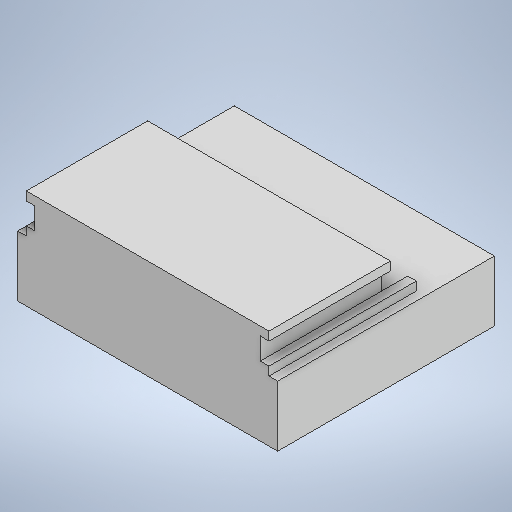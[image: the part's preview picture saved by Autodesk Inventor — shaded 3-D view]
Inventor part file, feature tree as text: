
AUTODESK INVENTOR PART (.ipt)
format: ipt  version: 2025.3 (Build 293356000, 356)  size: 224,768 bytes
history: native  units: mm
features: extrude x3, other x1, sketch x1
ambient origin geometry x8: Origin, YZ Plane, XZ Plane, XY Plane, X Axis, Y Axis, Z Axis, Center Point
bodies: Body1 (feature_tree)
feature tree (5):
  other  "솔리드1"
  sketch  "스케치1"
  extrude  "돌출1"  Depth=300.0mm
  extrude  "돌출2"  Depth=70.0mm
  extrude  "돌출3"  Depth=35.0mm
